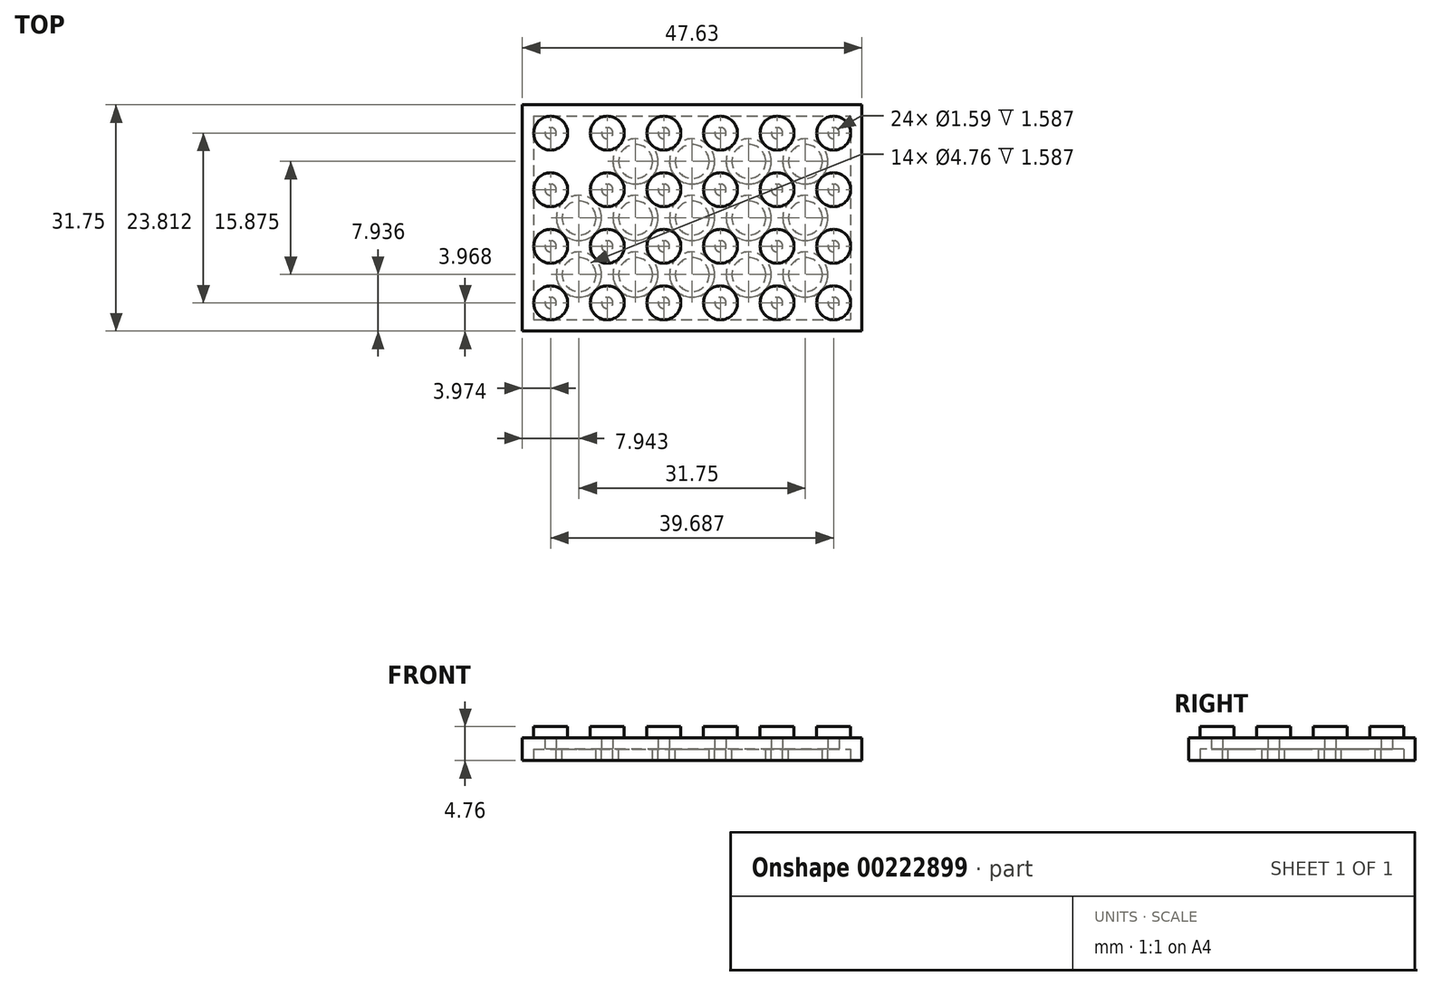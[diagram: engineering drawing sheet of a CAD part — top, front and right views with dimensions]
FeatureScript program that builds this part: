
annotation { "Feature Type Name" : "Feature", "Feature Type Description" : "" }
export const myFeature = defineFeature(function(context is Context, id is Id, definition is map)
    precondition{}
    {
        {
            var Q0;
            Q0=qCreatedBy(makeId("Top.planeOp"),FACE);
            var sketch = newSketch(context, id + "F0", { "sketchPlane" : qUnion([Q0])});
            skLineSegment(sketch, "E0.bottom", {"start": v(-15.88, 3.97) * mm, "end": v(31.75, 3.97) * mm});
            skLineSegment(sketch, "E0.top", {"start": v(-15.88, -27.78) * mm, "end": v(31.75, -27.78) * mm});
            skLineSegment(sketch, "E0.left", {"start": v(-15.88, 3.97) * mm, "end": v(-15.88, -27.78) * mm});
            skLineSegment(sketch, "E0.right", {"start": v(31.75, 3.97) * mm, "end": v(31.75, -27.78) * mm});
            skCircle(sketch, "E1", {"center": v(-11.9, 0) * mm, "radius": 2.38 * mm});
            skCircle(sketch, "E2.0.1.0", {"center": v(-11.9, -7.94) * mm, "radius": 2.38 * mm});
            skCircle(sketch, "E2.1.0.0", {"center": v(-3.97, 0) * mm, "radius": 2.38 * mm});
            skCircle(sketch, "E2.1.1.0", {"center": v(-3.97, -7.94) * mm, "radius": 2.38 * mm});
            skCircle(sketch, "E2.2.0.0", {"center": v(3.97, 0) * mm, "radius": 2.38 * mm});
            skCircle(sketch, "E2.2.1.0", {"center": v(3.97, -7.94) * mm, "radius": 2.38 * mm});
            skCircle(sketch, "E2.3.0.0", {"center": v(11.9, 0) * mm, "radius": 2.38 * mm});
            skCircle(sketch, "E2.3.1.0", {"center": v(11.9, -7.94) * mm, "radius": 2.38 * mm});
            skLineSegment(sketch, "E2.direction1", {"start": v(-11.9, 0) * mm, "end": v(-3.97, 0) * mm, "construction": true});
            skLineSegment(sketch, "E2.direction2", {"start": v(-11.9, 0) * mm, "end": v(-11.9, -7.94) * mm, "construction": true});
            skCircle(sketch, "E3.0.4.0", {"center": v(19.84, 0) * mm, "radius": 2.38 * mm});
            skCircle(sketch, "E3.0.4.1", {"center": v(19.84, -7.94) * mm, "radius": 2.38 * mm});
            skCircle(sketch, "E3.0.5.0", {"center": v(27.78, 0) * mm, "radius": 2.38 * mm});
            skCircle(sketch, "E3.0.5.1", {"center": v(27.78, -7.94) * mm, "radius": 2.38 * mm});
            skCircle(sketch, "E4.0.0.2", {"center": v(-11.9, -15.88) * mm, "radius": 2.38 * mm});
            skCircle(sketch, "E4.0.0.3", {"center": v(-11.9, -23.81) * mm, "radius": 2.38 * mm});
            skCircle(sketch, "E4.0.1.2", {"center": v(-3.97, -15.88) * mm, "radius": 2.38 * mm});
            skCircle(sketch, "E4.0.1.3", {"center": v(-3.97, -23.81) * mm, "radius": 2.38 * mm});
            skCircle(sketch, "E4.0.2.2", {"center": v(3.97, -15.88) * mm, "radius": 2.38 * mm});
            skCircle(sketch, "E4.0.2.3", {"center": v(3.97, -23.81) * mm, "radius": 2.38 * mm});
            skCircle(sketch, "E4.0.3.2", {"center": v(11.9, -15.88) * mm, "radius": 2.38 * mm});
            skCircle(sketch, "E4.0.3.3", {"center": v(11.9, -23.81) * mm, "radius": 2.38 * mm});
            skCircle(sketch, "E4.0.4.2", {"center": v(19.84, -15.88) * mm, "radius": 2.38 * mm});
            skCircle(sketch, "E4.0.4.3", {"center": v(19.84, -23.81) * mm, "radius": 2.38 * mm});
            skCircle(sketch, "E4.0.5.2", {"center": v(27.78, -15.88) * mm, "radius": 2.38 * mm});
            skCircle(sketch, "E4.0.5.3", {"center": v(27.78, -23.81) * mm, "radius": 2.38 * mm});
            skSolve(sketch);
        }
        {
            var Q0;
            Q0=makeQuery(id+"F0.imprint","IMPRINT",FACE,{"disambiguationData":[TD([[makeQuery(id+"F0.imprint","IMPRINT",EDGE,{"derivedFrom":sQuery(id+"F0.wireOp",EDGE,"E0.bottom")}),-1.0]])]});
            extrude(context, id + "F1", {"entities" : qUnion([Q0]), "depth" : 3.17 * mm});
        }
        {
            var Q0;
            Q0=makeQuery(id+"F0.imprint","IMPRINT",FACE,{"disambiguationData":[TD([[makeQuery(id+"F0.imprint","IMPRINT",EDGE,{"derivedFrom":sQuery(id+"F0.wireOp",EDGE,"E1")}),1.0]])]});
            var Q1;
            Q1=makeQuery(id+"F0.imprint","IMPRINT",FACE,{"disambiguationData":[TD([[makeQuery(id+"F0.imprint","IMPRINT",EDGE,{"derivedFrom":sQuery(id+"F0.wireOp",EDGE,"E2.0.1.0")}),1.0]])]});
            var Q2;
            Q2=makeQuery(id+"F0.imprint","IMPRINT",FACE,{"disambiguationData":[TD([[makeQuery(id+"F0.imprint","IMPRINT",EDGE,{"derivedFrom":sQuery(id+"F0.wireOp",EDGE,"E2.1.1.0")}),1.0]])]});
            var Q3;
            Q3=makeQuery(id+"F0.imprint","IMPRINT",FACE,{"disambiguationData":[TD([[makeQuery(id+"F0.imprint","IMPRINT",EDGE,{"derivedFrom":sQuery(id+"F0.wireOp",EDGE,"E2.1.0.0")}),1.0]])]});
            var Q4;
            Q4=makeQuery(id+"F0.imprint","IMPRINT",FACE,{"disambiguationData":[TD([[makeQuery(id+"F0.imprint","IMPRINT",EDGE,{"derivedFrom":sQuery(id+"F0.wireOp",EDGE,"E2.2.0.0")}),1.0]])]});
            var Q5;
            Q5=makeQuery(id+"F0.imprint","IMPRINT",FACE,{"disambiguationData":[TD([[makeQuery(id+"F0.imprint","IMPRINT",EDGE,{"derivedFrom":sQuery(id+"F0.wireOp",EDGE,"E2.2.1.0")}),1.0]])]});
            var Q6;
            Q6=makeQuery(id+"F0.imprint","IMPRINT",FACE,{"disambiguationData":[TD([[makeQuery(id+"F0.imprint","IMPRINT",EDGE,{"derivedFrom":sQuery(id+"F0.wireOp",EDGE,"E2.3.1.0")}),1.0]])]});
            var Q7;
            Q7=makeQuery(id+"F0.imprint","IMPRINT",FACE,{"disambiguationData":[TD([[makeQuery(id+"F0.imprint","IMPRINT",EDGE,{"derivedFrom":sQuery(id+"F0.wireOp",EDGE,"E2.3.0.0")}),1.0]])]});
            var Q8;
            Q8=makeQuery(id+"F0.imprint","IMPRINT",FACE,{"disambiguationData":[TD([[makeQuery(id+"F0.imprint","IMPRINT",EDGE,{"derivedFrom":sQuery(id+"F0.wireOp",EDGE,"E3.0.4.0")}),1.0]])]});
            var Q9;
            Q9=makeQuery(id+"F0.imprint","IMPRINT",FACE,{"disambiguationData":[TD([[makeQuery(id+"F0.imprint","IMPRINT",EDGE,{"derivedFrom":sQuery(id+"F0.wireOp",EDGE,"E3.0.5.0")}),1.0]])]});
            var Q10;
            Q10=makeQuery(id+"F0.imprint","IMPRINT",FACE,{"disambiguationData":[TD([[makeQuery(id+"F0.imprint","IMPRINT",EDGE,{"derivedFrom":sQuery(id+"F0.wireOp",EDGE,"E3.0.5.1")}),1.0]])]});
            var Q11;
            Q11=makeQuery(id+"F0.imprint","IMPRINT",FACE,{"disambiguationData":[TD([[makeQuery(id+"F0.imprint","IMPRINT",EDGE,{"derivedFrom":sQuery(id+"F0.wireOp",EDGE,"E3.0.4.1")}),1.0]])]});
            var Q12;
            Q12=makeQuery(id+"F0.imprint","IMPRINT",FACE,{"disambiguationData":[TD([[makeQuery(id+"F0.imprint","IMPRINT",EDGE,{"derivedFrom":sQuery(id+"F0.wireOp",EDGE,"E4.0.0.2")}),1.0]])]});
            var Q13;
            Q13=makeQuery(id+"F0.imprint","IMPRINT",FACE,{"disambiguationData":[TD([[makeQuery(id+"F0.imprint","IMPRINT",EDGE,{"derivedFrom":sQuery(id+"F0.wireOp",EDGE,"E4.0.1.2")}),1.0]])]});
            var Q14;
            Q14=makeQuery(id+"F0.imprint","IMPRINT",FACE,{"disambiguationData":[TD([[makeQuery(id+"F0.imprint","IMPRINT",EDGE,{"derivedFrom":sQuery(id+"F0.wireOp",EDGE,"E4.0.2.2")}),1.0]])]});
            var Q15;
            Q15=makeQuery(id+"F0.imprint","IMPRINT",FACE,{"disambiguationData":[TD([[makeQuery(id+"F0.imprint","IMPRINT",EDGE,{"derivedFrom":sQuery(id+"F0.wireOp",EDGE,"E4.0.3.2")}),1.0]])]});
            var Q16;
            Q16=makeQuery(id+"F0.imprint","IMPRINT",FACE,{"disambiguationData":[TD([[makeQuery(id+"F0.imprint","IMPRINT",EDGE,{"derivedFrom":sQuery(id+"F0.wireOp",EDGE,"E4.0.4.2")}),1.0]])]});
            var Q17;
            Q17=makeQuery(id+"F0.imprint","IMPRINT",FACE,{"disambiguationData":[TD([[makeQuery(id+"F0.imprint","IMPRINT",EDGE,{"derivedFrom":sQuery(id+"F0.wireOp",EDGE,"E4.0.5.2")}),1.0]])]});
            var Q18;
            Q18=makeQuery(id+"F0.imprint","IMPRINT",FACE,{"disambiguationData":[TD([[makeQuery(id+"F0.imprint","IMPRINT",EDGE,{"derivedFrom":sQuery(id+"F0.wireOp",EDGE,"E4.0.5.3")}),1.0]])]});
            var Q19;
            Q19=makeQuery(id+"F0.imprint","IMPRINT",FACE,{"disambiguationData":[TD([[makeQuery(id+"F0.imprint","IMPRINT",EDGE,{"derivedFrom":sQuery(id+"F0.wireOp",EDGE,"E4.0.4.3")}),1.0]])]});
            var Q20;
            Q20=makeQuery(id+"F0.imprint","IMPRINT",FACE,{"disambiguationData":[TD([[makeQuery(id+"F0.imprint","IMPRINT",EDGE,{"derivedFrom":sQuery(id+"F0.wireOp",EDGE,"E4.0.3.3")}),1.0]])]});
            var Q21;
            Q21=makeQuery(id+"F0.imprint","IMPRINT",FACE,{"disambiguationData":[TD([[makeQuery(id+"F0.imprint","IMPRINT",EDGE,{"derivedFrom":sQuery(id+"F0.wireOp",EDGE,"E4.0.2.3")}),1.0]])]});
            var Q22;
            Q22=makeQuery(id+"F0.imprint","IMPRINT",FACE,{"disambiguationData":[TD([[makeQuery(id+"F0.imprint","IMPRINT",EDGE,{"derivedFrom":sQuery(id+"F0.wireOp",EDGE,"E4.0.1.3")}),1.0]])]});
            var Q23;
            Q23=makeQuery(id+"F0.imprint","IMPRINT",FACE,{"disambiguationData":[TD([[makeQuery(id+"F0.imprint","IMPRINT",EDGE,{"derivedFrom":sQuery(id+"F0.wireOp",EDGE,"E4.0.0.3")}),1.0]])]});
            extrude(context, id + "F2", {"entities" : qUnion([Q0, Q1, Q2, Q3, Q4, Q5, Q6, Q7, Q8, Q9, Q10, Q11, Q12, Q13, Q14, Q15, Q16, Q17, Q18, Q19, Q20, Q21, Q22, Q23]), "operationType" : NewBodyOperationType.ADD, "depth" : 4.76 * mm});
        }
        {
            var Q0;
            {var subQ0=sQuery(id+"F0.wireOp",EDGE,"8b71ed98-f0e1-4300-85cb-82ad82c44b3e0.MirrorC");var subQ1=sQuery(id+"F0.wireOp",EDGE,"E1");Q0=makeQuery(id+"F2.boolean.opBoolean","MERGE",FACE,{"derivedFrom":[makeQuery(id+"F1.opExtrude","CAP_FACE",FACE,{"disambiguationData":[OSD([sQuery(id+"F0.wireOp",EDGE,"E0.bottom"),sQuery(id+"F0.wireOp",EDGE,"E0.top"),sQuery(id+"F0.wireOp",EDGE,"E0.left"),sQuery(id+"F0.wireOp",EDGE,"E0.right"),subQ1,subQ0])],"isStart":true}),makeQuery(id+"F2.opExtrude","CAP_FACE",FACE,{"disambiguationData":[OSD([subQ1])],"isStart":true}),makeQuery(id+"F2.opExtrude","CAP_FACE",FACE,{"disambiguationData":[OSD([subQ0])],"isStart":true})]});}
            shell(context, id + "F3", {"entities" : qUnion([Q0]), "thickness" : 1.59 * mm});
        }
        {
            var Q0;
            Q0=makeQuery(id+"F3.opShell","OFFSET_FACE",FACE,{"disambiguationData":[OSD([sQuery(id+"F0.wireOp",EDGE,"E0.bottom"),sQuery(id+"F0.wireOp",EDGE,"E0.top"),sQuery(id+"F0.wireOp",EDGE,"E0.left"),sQuery(id+"F0.wireOp",EDGE,"E0.right"),sQuery(id+"F0.wireOp",EDGE,"E1"),sQuery(id+"F0.wireOp",EDGE,"E2.0.1.0"),sQuery(id+"F0.wireOp",EDGE,"E2.1.0.0"),sQuery(id+"F0.wireOp",EDGE,"E2.1.1.0"),sQuery(id+"F0.wireOp",EDGE,"E2.2.0.0"),sQuery(id+"F0.wireOp",EDGE,"E2.2.1.0"),sQuery(id+"F0.wireOp",EDGE,"E2.3.0.0"),sQuery(id+"F0.wireOp",EDGE,"E2.3.1.0")])]});
            var sketch = newSketch(context, id + "F4", { "sketchPlane" : qUnion([Q0])});
            skLineSegment(sketch, "E5", {"start": v(-11.9, 7.94) * mm, "end": v(-3.97, 0) * mm});
            skCircle(sketch, "E6", {"center": v(-7.94, 3.97) * mm, "radius": 3.18 * mm});
            skCircle(sketch, "E7.0", {"center": v(-7.94, 3.97) * mm, "radius": 2.38 * mm});
            skCircle(sketch, "E8.0.1.0", {"center": v(-7.94, 11.9) * mm, "radius": 3.18 * mm});
            skCircle(sketch, "E8.0.1.1", {"center": v(-7.94, 11.9) * mm, "radius": 2.38 * mm});
            skCircle(sketch, "E8.0.2.0", {"center": v(-7.94, 19.84) * mm, "radius": 3.18 * mm});
            skCircle(sketch, "E8.0.2.1", {"center": v(-7.94, 19.84) * mm, "radius": 2.38 * mm});
            skCircle(sketch, "E8.1.0.0", {"center": v(0, 3.97) * mm, "radius": 3.18 * mm});
            skCircle(sketch, "E8.1.0.1", {"center": v(0, 3.97) * mm, "radius": 2.38 * mm});
            skCircle(sketch, "E8.1.1.0", {"center": v(0, 11.9) * mm, "radius": 3.18 * mm});
            skCircle(sketch, "E8.1.1.1", {"center": v(0, 11.9) * mm, "radius": 2.38 * mm});
            skCircle(sketch, "E8.1.2.0", {"center": v(0, 19.84) * mm, "radius": 3.18 * mm});
            skCircle(sketch, "E8.1.2.1", {"center": v(0, 19.84) * mm, "radius": 2.38 * mm});
            skCircle(sketch, "E8.2.0.0", {"center": v(7.94, 3.97) * mm, "radius": 3.18 * mm});
            skCircle(sketch, "E8.2.0.1", {"center": v(7.94, 3.97) * mm, "radius": 2.38 * mm});
            skCircle(sketch, "E8.2.1.0", {"center": v(7.94, 11.9) * mm, "radius": 3.18 * mm});
            skCircle(sketch, "E8.2.1.1", {"center": v(7.94, 11.9) * mm, "radius": 2.38 * mm});
            skCircle(sketch, "E8.2.2.0", {"center": v(7.94, 19.84) * mm, "radius": 3.18 * mm});
            skCircle(sketch, "E8.2.2.1", {"center": v(7.94, 19.84) * mm, "radius": 2.38 * mm});
            skCircle(sketch, "E8.3.0.0", {"center": v(15.88, 3.97) * mm, "radius": 3.18 * mm});
            skCircle(sketch, "E8.3.0.1", {"center": v(15.88, 3.97) * mm, "radius": 2.38 * mm});
            skCircle(sketch, "E8.3.1.0", {"center": v(15.88, 11.9) * mm, "radius": 3.18 * mm});
            skCircle(sketch, "E8.3.1.1", {"center": v(15.88, 11.9) * mm, "radius": 2.38 * mm});
            skCircle(sketch, "E8.3.2.0", {"center": v(15.88, 19.84) * mm, "radius": 3.18 * mm});
            skCircle(sketch, "E8.3.2.1", {"center": v(15.88, 19.84) * mm, "radius": 2.38 * mm});
            skCircle(sketch, "E8.4.0.0", {"center": v(23.81, 3.97) * mm, "radius": 3.18 * mm});
            skCircle(sketch, "E8.4.0.1", {"center": v(23.81, 3.97) * mm, "radius": 2.38 * mm});
            skCircle(sketch, "E8.4.1.0", {"center": v(23.81, 11.9) * mm, "radius": 3.18 * mm});
            skCircle(sketch, "E8.4.1.1", {"center": v(23.81, 11.9) * mm, "radius": 2.38 * mm});
            skCircle(sketch, "E8.4.2.0", {"center": v(23.81, 19.84) * mm, "radius": 3.18 * mm});
            skCircle(sketch, "E8.4.2.1", {"center": v(23.81, 19.84) * mm, "radius": 2.38 * mm});
            skLineSegment(sketch, "E8.direction1", {"start": v(-7.94, 3.97) * mm, "end": v(0, 3.97) * mm, "construction": true});
            skLineSegment(sketch, "E8.direction2", {"start": v(-7.94, 3.97) * mm, "end": v(-7.94, 11.9) * mm, "construction": true});
            skSolve(sketch);
        }
        {
            var Q0;
            Q0=makeQuery(id+"F4.imprint","IMPRINT",FACE,{"disambiguationData":[TD([[makeQuery(id+"F4.imprint","IMPRINT",EDGE,{"derivedFrom":sQuery(id+"F4.wireOp",EDGE,"E8.0.2.0")}),1.0]])]});
            var Q1;
            Q1=makeQuery(id+"F4.imprint","IMPRINT",FACE,{"disambiguationData":[TD([[makeQuery(id+"F4.imprint","IMPRINT",EDGE,{"derivedFrom":sQuery(id+"F4.wireOp",EDGE,"E8.1.2.0")}),1.0]])]});
            var Q2;
            Q2=makeQuery(id+"F4.imprint","IMPRINT",FACE,{"disambiguationData":[TD([[makeQuery(id+"F4.imprint","IMPRINT",EDGE,{"derivedFrom":sQuery(id+"F4.wireOp",EDGE,"E8.2.2.0")}),1.0]])]});
            var Q3;
            Q3=makeQuery(id+"F4.imprint","IMPRINT",FACE,{"disambiguationData":[TD([[makeQuery(id+"F4.imprint","IMPRINT",EDGE,{"derivedFrom":sQuery(id+"F4.wireOp",EDGE,"E8.3.2.0")}),1.0]])]});
            var Q4;
            Q4=makeQuery(id+"F4.imprint","IMPRINT",FACE,{"disambiguationData":[TD([[makeQuery(id+"F4.imprint","IMPRINT",EDGE,{"derivedFrom":sQuery(id+"F4.wireOp",EDGE,"E8.4.2.0")}),1.0]])]});
            var Q5;
            Q5=makeQuery(id+"F4.imprint","IMPRINT",FACE,{"disambiguationData":[TD([[makeQuery(id+"F4.imprint","IMPRINT",EDGE,{"derivedFrom":sQuery(id+"F4.wireOp",EDGE,"E8.4.1.0")}),1.0]])]});
            var Q6;
            Q6=makeQuery(id+"F4.imprint","IMPRINT",FACE,{"disambiguationData":[TD([[makeQuery(id+"F4.imprint","IMPRINT",EDGE,{"derivedFrom":sQuery(id+"F4.wireOp",EDGE,"E8.3.1.0")}),1.0]])]});
            var Q7;
            Q7=makeQuery(id+"F4.imprint","IMPRINT",FACE,{"disambiguationData":[TD([[makeQuery(id+"F4.imprint","IMPRINT",EDGE,{"derivedFrom":sQuery(id+"F4.wireOp",EDGE,"E8.2.1.0")}),1.0]])]});
            var Q8;
            Q8=makeQuery(id+"F4.imprint","IMPRINT",FACE,{"disambiguationData":[TD([[makeQuery(id+"F4.imprint","IMPRINT",EDGE,{"derivedFrom":sQuery(id+"F4.wireOp",EDGE,"E8.1.1.0")}),1.0]])]});
            var Q9;
            Q9=makeQuery(id+"F4.imprint","IMPRINT",FACE,{"disambiguationData":[TD([[makeQuery(id+"F4.imprint","IMPRINT",EDGE,{"derivedFrom":sQuery(id+"F4.wireOp",EDGE,"E8.0.1.0")}),1.0]])]});
            var Q10;
            {var subQ0=sQuery(id+"F4.wireOp",EDGE,"E6");var subQ1=sQuery(id+"F4.wireOp",EDGE,"E5");var subQ2=makeQuery(id+"F4.imprint","INTERSECT",VERTEX,{"disambiguationData":[OD(0.0)],"derivedFrom":[subQ1,subQ0]});Q10=makeQuery(id+"F4.imprint","IMPRINT",FACE,{"disambiguationData":[TD([[makeQuery(id+"F4.imprint","IMPRINT",EDGE,{"disambiguationData":[TD([[subQ2,-1.0]])],"derivedFrom":subQ1}),1.0]])]});}
            var Q11;
            {var subQ0=sQuery(id+"F4.wireOp",EDGE,"E6");var subQ1=sQuery(id+"F4.wireOp",EDGE,"E5");var subQ2=makeQuery(id+"F4.imprint","INTERSECT",VERTEX,{"disambiguationData":[OD(0.0)],"derivedFrom":[subQ1,subQ0]});Q11=makeQuery(id+"F4.imprint","IMPRINT",FACE,{"disambiguationData":[TD([[makeQuery(id+"F4.imprint","IMPRINT",EDGE,{"disambiguationData":[TD([[subQ2,-1.0]])],"derivedFrom":subQ1}),-1.0]])]});}
            var Q12;
            Q12=makeQuery(id+"F4.imprint","IMPRINT",FACE,{"disambiguationData":[TD([[makeQuery(id+"F4.imprint","IMPRINT",EDGE,{"derivedFrom":sQuery(id+"F4.wireOp",EDGE,"E8.1.0.0")}),1.0]])]});
            var Q13;
            Q13=makeQuery(id+"F4.imprint","IMPRINT",FACE,{"disambiguationData":[TD([[makeQuery(id+"F4.imprint","IMPRINT",EDGE,{"derivedFrom":sQuery(id+"F4.wireOp",EDGE,"E8.2.0.0")}),1.0]])]});
            var Q14;
            Q14=makeQuery(id+"F4.imprint","IMPRINT",FACE,{"disambiguationData":[TD([[makeQuery(id+"F4.imprint","IMPRINT",EDGE,{"derivedFrom":sQuery(id+"F4.wireOp",EDGE,"E8.3.0.0")}),1.0]])]});
            var Q15;
            Q15=makeQuery(id+"F4.imprint","IMPRINT",FACE,{"disambiguationData":[TD([[makeQuery(id+"F4.imprint","IMPRINT",EDGE,{"derivedFrom":sQuery(id+"F4.wireOp",EDGE,"E8.4.0.0")}),1.0]])]});
            extrude(context, id + "F5", {"entities" : qUnion([Q0, Q1, Q2, Q3, Q4, Q5, Q6, Q7, Q8, Q9, Q10, Q11, Q12, Q13, Q14, Q15]), "operationType" : NewBodyOperationType.ADD, "depth" : 1.59 * mm});
        }
    });
